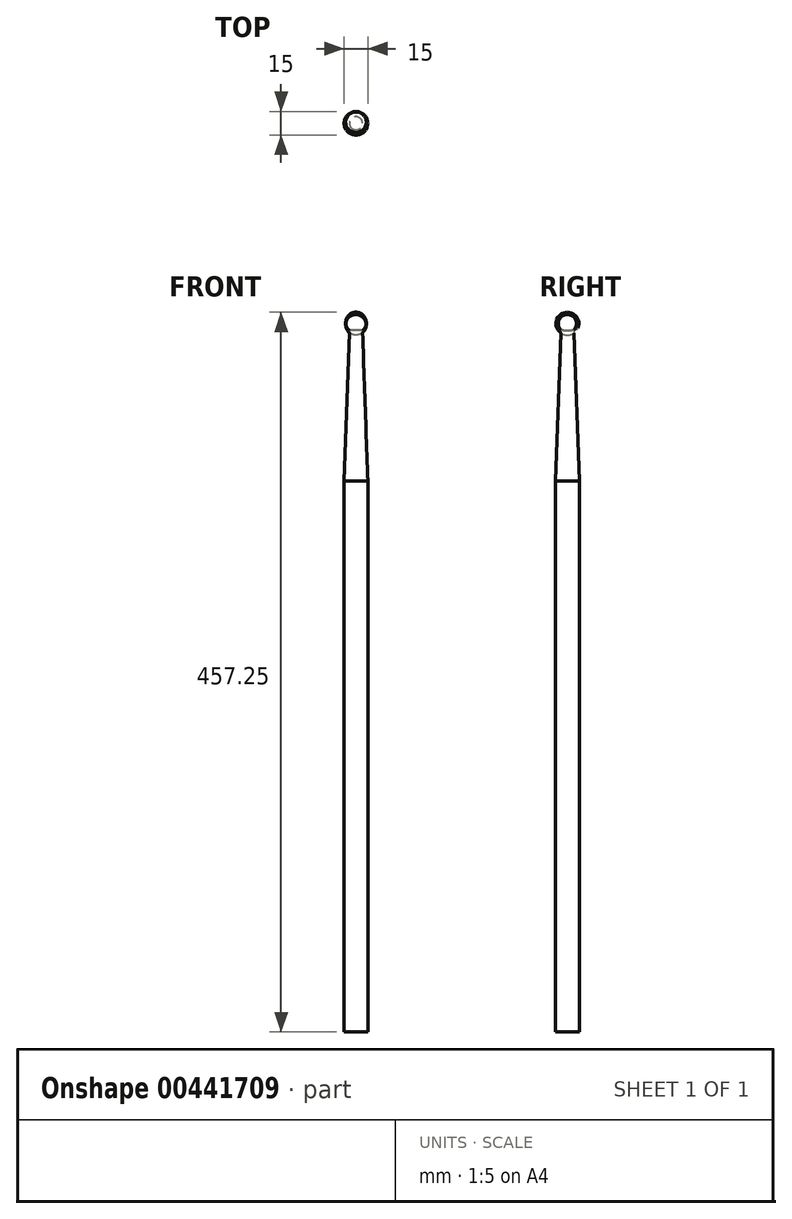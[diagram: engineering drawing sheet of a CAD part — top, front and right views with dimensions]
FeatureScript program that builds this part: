
annotation { "Feature Type Name" : "Feature", "Feature Type Description" : "" }
export const myFeature = defineFeature(function(context is Context, id is Id, definition is map)
    precondition{}
    {
        {
            var Q0;
            Q0=qCreatedBy(makeId("Top.planeOp"),FACE);
            var sketch = newSketch(context, id + "F0", { "sketchPlane" : qUnion([Q0])});
            skCircle(sketch, "E0", {"center": v(0, 0) * mm, "radius": 7.5 * mm});
            skSolve(sketch);
        }
        {
            var Q0;
            Q0 = qSketchRegion(id + "F0", true);
            extrude(context, id + "F1", {"entities" : qUnion([Q0]), "depth" : 350 * mm});
        }
        {
            var Q0;
            Q0=makeQuery(id+"F1.opExtrude","CAP_FACE",FACE,{"disambiguationData":[OSD([sQuery(id+"F0.wireOp",EDGE,"E0")])],"isStart":false});
            extrude(context, id + "F2", {"entities" : qUnion([Q0]), "operationType" : NewBodyOperationType.ADD, "depth" : 100 * mm, "hasDraft" : true, "draftAngle" : 2 * degree, "draftPullDirection" : true});
        }
        {
            var Q0;
            Q0=makeQuery(id+"F2.opExtrude","CAP_FACE",FACE,{"disambiguationData":[OSD([sQuery(id+"F0.wireOp",EDGE,"E0")])],"isStart":false});
            var sketch = newSketch(context, id + "F3", { "sketchPlane" : qUnion([Q0])});
            skLineSegment(sketch, "E1", {"start": v(-8.11, 0) * mm, "end": v(7.7, 0) * mm, "construction": true});
            skArc(sketch, "E2", {"start": v(-6.5, 0) * mm, "mid": v(0, -5.83) * mm, "end": v(6.5, 0) * mm});
            skLineSegment(sketch, "E3", {"start": v(0, 6) * mm, "end": v(0, -7.53) * mm, "construction": true});
            skLineSegment(sketch, "E4", {"start": v(-6.5, 0) * mm, "end": v(6.5, 0) * mm});
            skSolve(sketch);
        }
        {
            var Q0;
            Q0 = qSketchRegion(id + "F3", true);
            var Q1;
            Q1=sQuery(id+"F3.wireOp",EDGE,"E1");
            revolve(context, id + "F4", {"operationType" : NewBodyOperationType.ADD, "entities" : qUnion([Q0]), "axis" : qUnion([Q1]), "revolveType" : RevolveType.ONE_DIRECTION, "oppositeDirection" : true, "angle" : 360 * degree});
        }
    });
